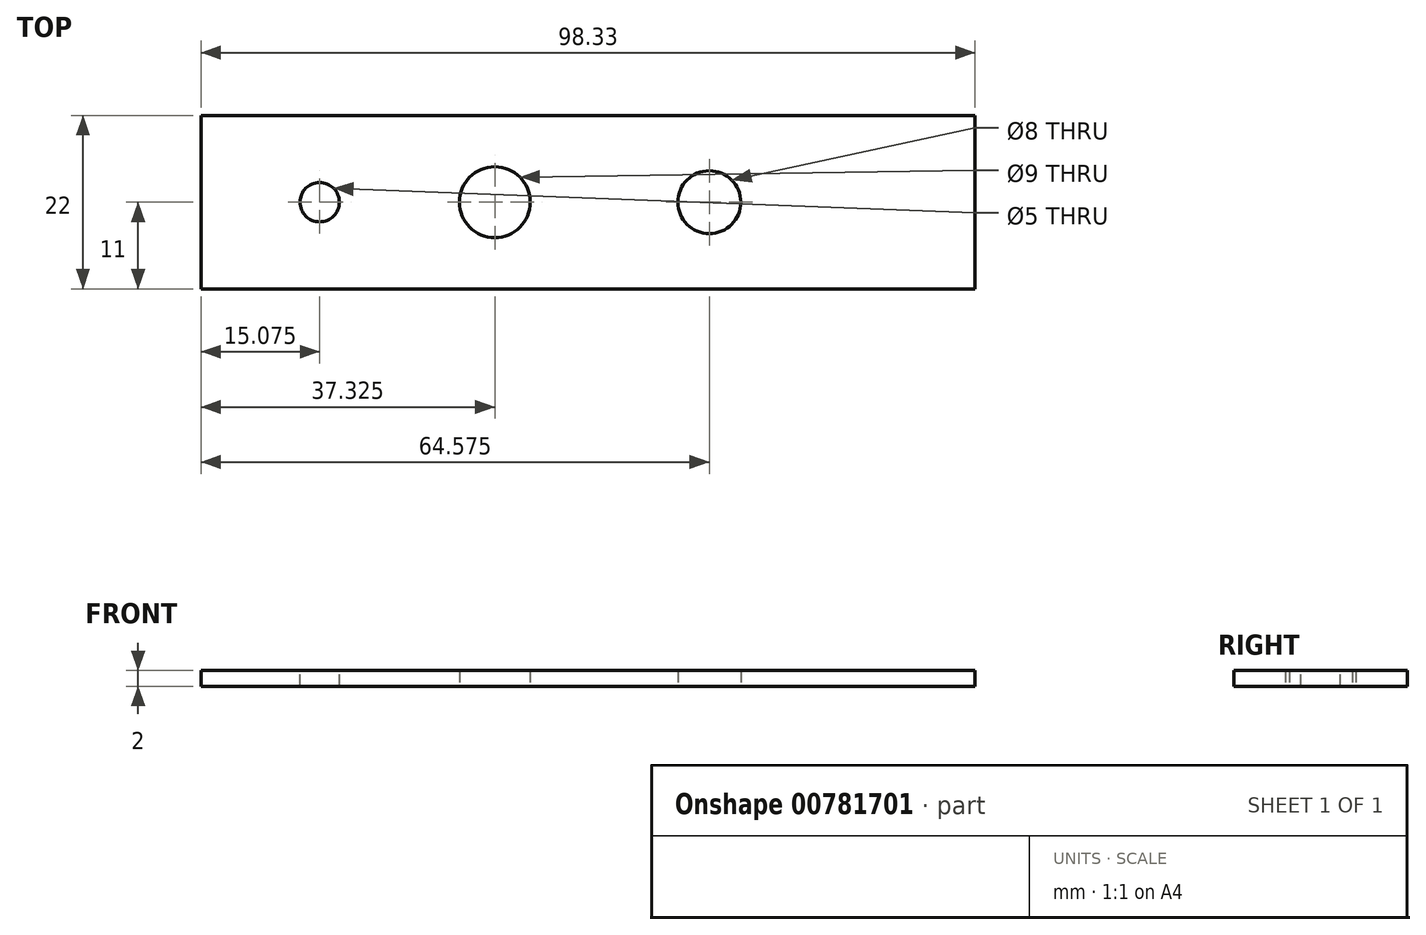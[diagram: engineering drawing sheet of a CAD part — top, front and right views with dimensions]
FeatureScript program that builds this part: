
annotation { "Feature Type Name" : "Feature", "Feature Type Description" : "" }
export const myFeature = defineFeature(function(context is Context, id is Id, definition is map)
    precondition{}
    {
        {
            var Q0;
            Q0=qCreatedBy(makeId("Top.planeOp"),FACE);
            var sketch = newSketch(context, id + "F0", { "sketchPlane" : qUnion([Q0])});
            skLineSegment(sketch, "E0.bottom", {"start": v(-48.33, 11) * mm, "end": v(50, 11) * mm});
            skLineSegment(sketch, "E0.top", {"start": v(-48.33, -11) * mm, "end": v(50, -11) * mm});
            skLineSegment(sketch, "E0.left", {"start": v(-48.33, 11) * mm, "end": v(-48.33, -11) * mm});
            skLineSegment(sketch, "E0.right", {"start": v(50, 11) * mm, "end": v(50, -11) * mm});
            skSolve(sketch);
        }
        {
            var Q0;
            Q0=makeQuery(id+"F0.imprint","IMPRINT",FACE,{"disambiguationData":[TD([[makeQuery(id+"F0.imprint","IMPRINT",EDGE,{"derivedFrom":sQuery(id+"F0.wireOp",EDGE,"E0.bottom")}),-1.0]])]});
            var sketch = newSketch(context, id + "F1", { "sketchPlane" : qUnion([Q0])});
            skCircle(sketch, "E1", {"center": v(-11, 0) * mm, "radius": 4.5 * mm});
            skCircle(sketch, "E2", {"center": v(16.25, 0) * mm, "radius": 4 * mm});
            skSolve(sketch);
        }
        {
            var Q0;
            Q0=makeQuery(id+"F1.imprint","IMPRINT",FACE,{"disambiguationData":[TD([[makeQuery(id+"F1.imprint","IMPRINT",EDGE,{"derivedFrom":sQuery(id+"F1.wireOp",EDGE,"E1")}),-1.0]])]});
            extrude(context, id + "F2", {"entities" : qUnion([Q0]), "depth" : 2 * mm, "offsetDistance" : 25 * mm});
        }
        {
            var Q0;
            Q0=makeQuery(id+"F2.opExtrude","CAP_FACE",FACE,{"disambiguationData":[OSD([sQuery(id+"F0.wireOp",EDGE,"E0.bottom"),sQuery(id+"F0.wireOp",EDGE,"E0.top"),sQuery(id+"F0.wireOp",EDGE,"E0.left"),sQuery(id+"F0.wireOp",EDGE,"E0.right"),sQuery(id+"F1.wireOp",EDGE,"E1"),sQuery(id+"F1.wireOp",EDGE,"E2")])],"isStart":false});
            var sketch = newSketch(context, id + "F3", { "sketchPlane" : qUnion([Q0])});
            skCircle(sketch, "E3", {"center": v(-33.25, 0) * mm, "radius": 2.5 * mm});
            skSolve(sketch);
        }
        {
            var Q0;
            Q0 = qSketchRegion(id + "F3", true);
            extrude(context, id + "F4", {"entities" : qUnion([Q0]), "operationType" : NewBodyOperationType.REMOVE, "oppositeDirection" : true, "depth" : 25 * mm, "offsetDistance" : 25 * mm});
        }
    });
